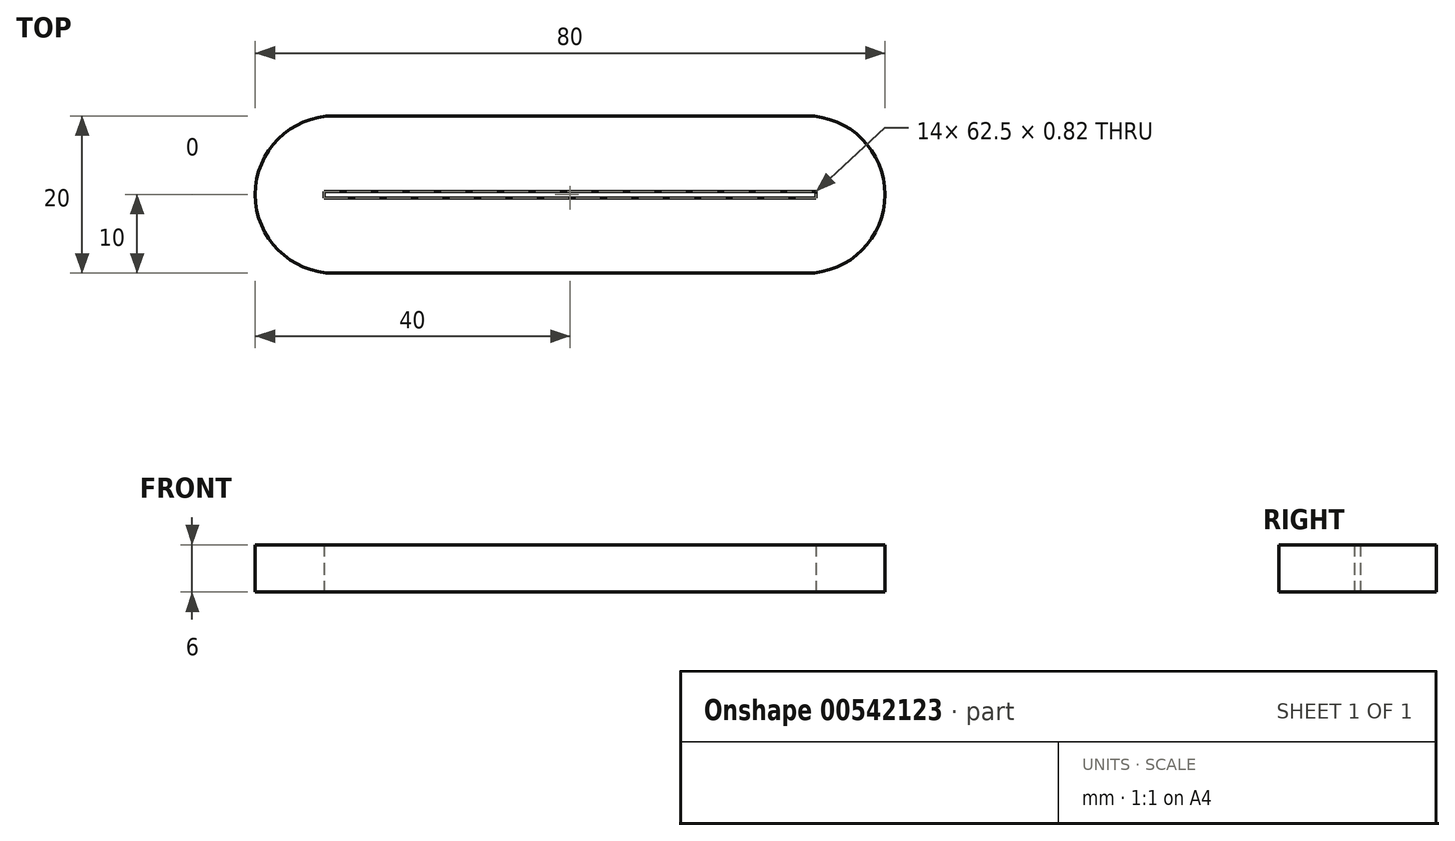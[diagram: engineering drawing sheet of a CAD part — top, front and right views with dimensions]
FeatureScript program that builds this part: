
annotation { "Feature Type Name" : "Feature", "Feature Type Description" : "" }
export const myFeature = defineFeature(function(context is Context, id is Id, definition is map)
    precondition{}
    {
        {
            var Q0;
            Q0=qCreatedBy(makeId("Top.planeOp"),FACE);
            var sketch = newSketch(context, id + "F0", { "sketchPlane" : qUnion([Q0])});
            skLineSegment(sketch, "E0.bottom", {"start": v(-40, 10) * mm, "end": v(40, 10) * mm});
            skLineSegment(sketch, "E0.top", {"start": v(-40, -10) * mm, "end": v(40, -10) * mm});
            skLineSegment(sketch, "E0.left", {"start": v(-40, 10) * mm, "end": v(-40, -10) * mm});
            skLineSegment(sketch, "E0.right", {"start": v(40, 10) * mm, "end": v(40, -10) * mm});
            skPoint(sketch, "E0.middle", {"position": v(0, 0) * mm});
            skLineSegment(sketch, "E1.bottom", {"start": v(-31.25, 0.41) * mm, "end": v(31.25, 0.41) * mm});
            skLineSegment(sketch, "E1.top", {"start": v(-31.25, -0.41) * mm, "end": v(31.25, -0.41) * mm});
            skLineSegment(sketch, "E1.left", {"start": v(-31.25, 0.41) * mm, "end": v(-31.25, -0.41) * mm});
            skLineSegment(sketch, "E1.right", {"start": v(31.25, 0.41) * mm, "end": v(31.25, -0.41) * mm});
            skSolve(sketch);
        }
        {
            var Q0;
            Q0=makeQuery(id+"F0.imprint","IMPRINT",FACE,{"disambiguationData":[TD([[makeQuery(id+"F0.imprint","IMPRINT",EDGE,{"derivedFrom":sQuery(id+"F0.wireOp",EDGE,"E0.bottom")}),-1.0]])]});
            extrude(context, id + "F1", {"entities" : qUnion([Q0]), "depth" : 6 * mm, "offsetDistance" : 25 * mm});
        }
        {
            var Q0;
            Q0=makeQuery(id+"F1.opExtrude","SWEPT_EDGE",EDGE,{"disambiguationData":[OSD([sQuery(id+"F0.wireOp",EDGE,"E0.bottom"),sQuery(id+"F0.wireOp",EDGE,"E0.left")])]});
            var Q1;
            Q1=makeQuery(id+"F1.opExtrude","SWEPT_EDGE",EDGE,{"disambiguationData":[OSD([sQuery(id+"F0.wireOp",EDGE,"E0.top"),sQuery(id+"F0.wireOp",EDGE,"E0.left")])]});
            var Q2;
            Q2=makeQuery(id+"F1.opExtrude","SWEPT_EDGE",EDGE,{"disambiguationData":[OSD([sQuery(id+"F0.wireOp",EDGE,"E0.bottom"),sQuery(id+"F0.wireOp",EDGE,"E0.right")])]});
            var Q3;
            Q3=makeQuery(id+"F1.opExtrude","SWEPT_EDGE",EDGE,{"disambiguationData":[OSD([sQuery(id+"F0.wireOp",EDGE,"E0.top"),sQuery(id+"F0.wireOp",EDGE,"E0.right")])]});
            fillet(context, id + "F2", {"entities" : qUnion([Q0, Q1, Q2, Q3]), "radius" : 10 * mm, "tangentPropagation" : true, "allowEdgeOverflow" : false});
        }
    });
